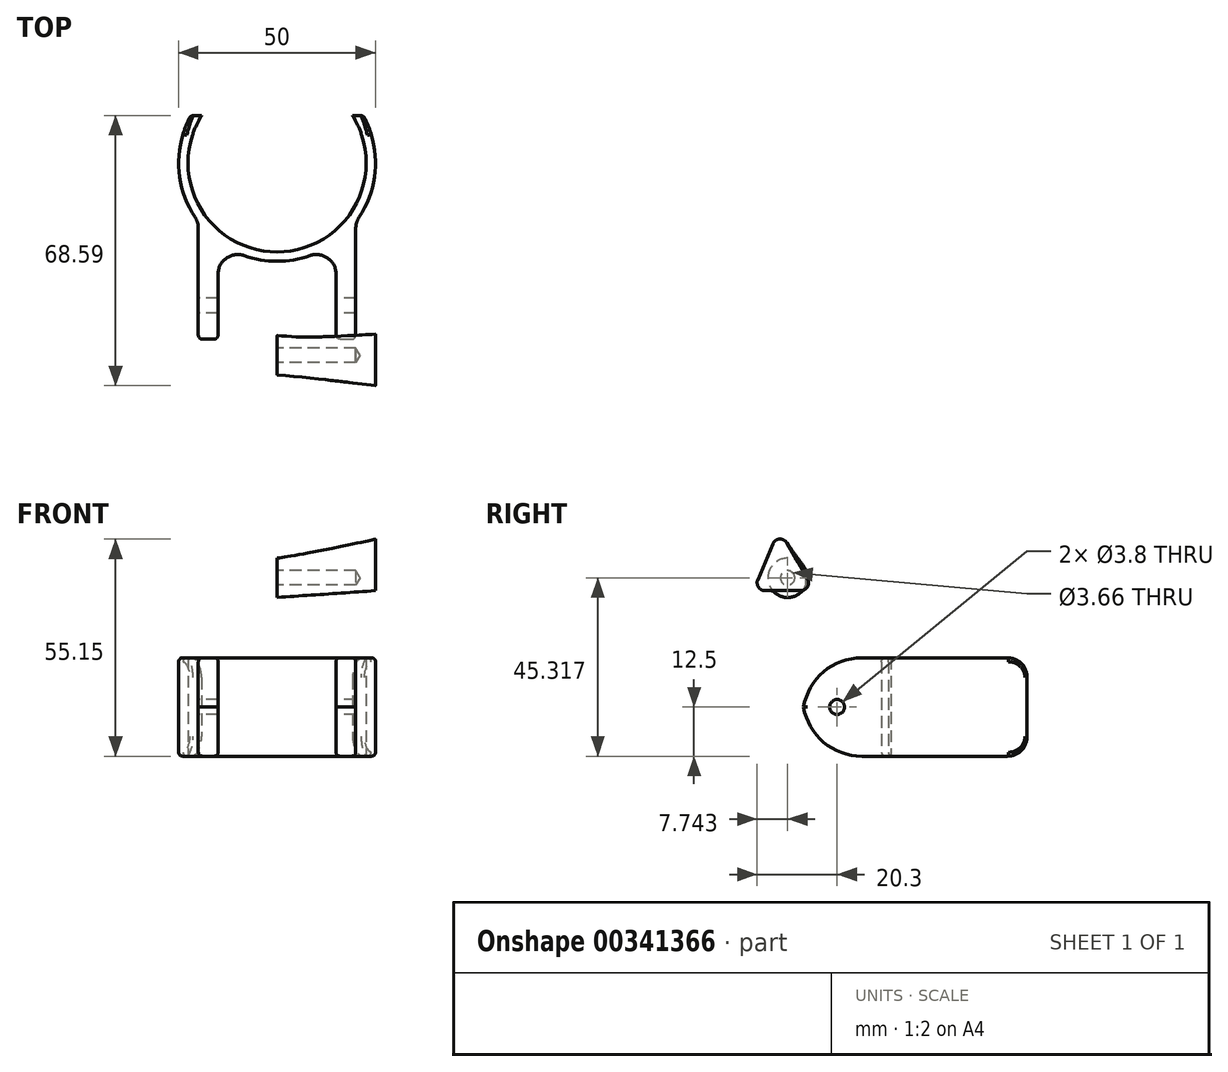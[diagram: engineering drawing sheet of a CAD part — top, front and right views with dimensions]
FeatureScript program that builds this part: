
annotation { "Feature Type Name" : "Feature", "Feature Type Description" : "" }
export const myFeature = defineFeature(function(context is Context, id is Id, definition is map)
    precondition{}
    {
        {
            var Q0;
            Q0=qCreatedBy(makeId("Top.planeOp"),FACE);
            var sketch = newSketch(context, id + "F0", { "sketchPlane" : qUnion([Q0])});
            skArc(sketch, "E0", {"start": v(-19.18, 12) * mm, "mid": v(0, -22.62) * mm, "end": v(19.18, 12) * mm});
            skArc(sketch, "E1", {"start": v(-21.93, 12) * mm, "mid": v(0, -25) * mm, "end": v(21.93, 12) * mm});
            skLineSegment(sketch, "E2", {"start": v(-19.18, 12) * mm, "end": v(-21.93, 12) * mm});
            skLineSegment(sketch, "E3", {"start": v(19.18, 12) * mm, "end": v(21.93, 12) * mm});
            skSolve(sketch);
        }
        {
            var Q0;
            Q0=makeQuery(id+"F0.imprint","IMPRINT",FACE,{"disambiguationData":[TD([[makeQuery(id+"F0.imprint","IMPRINT",EDGE,{"derivedFrom":sQuery(id+"F0.wireOp",EDGE,"E0")}),-1.0]])]});
            extrude(context, id + "F1", {"entities" : qUnion([Q0]), "depth" : 25 * mm});
        }
        {
            var Q0;
            Q0=qCreatedBy(makeId("Front.planeOp"),FACE);
            var sketch = newSketch(context, id + "F2", { "sketchPlane" : qUnion([Q0])});
            skLineSegment(sketch, "E4.bottom", {"start": v(-20, 25) * mm, "end": v(-15, 25) * mm});
            skLineSegment(sketch, "E4.top", {"start": v(-20, 0) * mm, "end": v(-15, 0) * mm});
            skLineSegment(sketch, "E4.left", {"start": v(-20, 25) * mm, "end": v(-20, 0) * mm});
            skLineSegment(sketch, "E4.right", {"start": v(-15, 25) * mm, "end": v(-15, 0) * mm});
            skLineSegment(sketch, "E5.bottom", {"start": v(15, 25) * mm, "end": v(20, 25) * mm});
            skLineSegment(sketch, "E5.top", {"start": v(15, 0) * mm, "end": v(20, 0) * mm});
            skLineSegment(sketch, "E5.left", {"start": v(15, 25) * mm, "end": v(15, 0) * mm});
            skLineSegment(sketch, "E5.right", {"start": v(20, 25) * mm, "end": v(20, 0) * mm});
            skSolve(sketch);
        }
        {
            var Q0;
            Q0=makeQuery(id+"F2.imprint","IMPRINT",FACE,{"disambiguationData":[TD([[makeQuery(id+"F2.imprint","IMPRINT",EDGE,{"derivedFrom":sQuery(id+"F2.wireOp",EDGE,"E4.bottom")}),-1.0]])]});
            var Q1;
            Q1=makeQuery(id+"F2.imprint","IMPRINT",FACE,{"disambiguationData":[TD([[makeQuery(id+"F2.imprint","IMPRINT",EDGE,{"derivedFrom":sQuery(id+"F2.wireOp",EDGE,"E5.bottom")}),-1.0]])]});
            var Q2;
            Q2=makeQuery(id+"F1.opExtrude","SWEPT_FACE",FACE,{"disambiguationData":[OSD([sQuery(id+"F0.wireOp",EDGE,"E0")])]});
            extrude(context, id + "F3", {"entities" : qUnion([Q0, Q1]), "endBoundEntityFace" : qUnion([Q2]), "depth" : 45 * mm, "hasSecondDirection" : true, "secondDirectionBound" : BoundingType.UP_TO_NEXT, "secondDirectionOppositeDirection" : false, "secondDirectionDepth" : 25 * mm});
        }
        {
            var Q0;
            Q0=makeQuery(id+"F3.opExtrude","SWEPT_BODY",BODY,{"disambiguationData":[OSD([sQuery(id+"F2.wireOp",EDGE,"E5.bottom"),sQuery(id+"F2.wireOp",EDGE,"E5.top"),sQuery(id+"F2.wireOp",EDGE,"E5.left"),sQuery(id+"F2.wireOp",EDGE,"E5.right")])]});
            var Q1;
            Q1=makeQuery(id+"F3.opExtrude","SWEPT_BODY",BODY,{"disambiguationData":[OSD([sQuery(id+"F2.wireOp",EDGE,"E4.bottom"),sQuery(id+"F2.wireOp",EDGE,"E4.top"),sQuery(id+"F2.wireOp",EDGE,"E4.left"),sQuery(id+"F2.wireOp",EDGE,"E4.right")])]});
            var Q2;
            Q2=makeQuery(id+"F1.opExtrude","SWEPT_BODY",BODY,{"disambiguationData":[OSD([sQuery(id+"F0.wireOp",EDGE,"E0"),sQuery(id+"F0.wireOp",EDGE,"E1"),sQuery(id+"F0.wireOp",EDGE,"E2"),sQuery(id+"F0.wireOp",EDGE,"E3")])]});
            booleanBodies(context, id + "F4", {"operationType" : BooleanOperationType.UNION, "tools" : qUnion([Q0, Q1, Q2])});
        }
        {
            var Q0;
            Q0=makeQuery(id+"F3.opExtrude","CAP_EDGE",EDGE,{"disambiguationData":[OSD([sQuery(id+"F2.wireOp",EDGE,"E4.bottom")])],"isStart":false});
            var Q1;
            Q1=makeQuery(id+"F3.opExtrude","CAP_EDGE",EDGE,{"disambiguationData":[OSD([sQuery(id+"F2.wireOp",EDGE,"E5.bottom")])],"isStart":false});
            var Q2;
            Q2=makeQuery(id+"F3.opExtrude","CAP_EDGE",EDGE,{"disambiguationData":[OSD([sQuery(id+"F2.wireOp",EDGE,"E4.top")])],"isStart":false});
            var Q3;
            Q3=makeQuery(id+"F3.opExtrude","CAP_EDGE",EDGE,{"disambiguationData":[OSD([sQuery(id+"F2.wireOp",EDGE,"E5.top")])],"isStart":false});
            fillet(context, id + "F5", {"entities" : qUnion([Q0, Q1, Q2, Q3]), "radius" : 15 * mm, "tangentPropagation" : true, "allowEdgeOverflow" : false});
        }
        {
            var Q0;
            Q0=makeQuery(id+"F3.opExtrude","SWEPT_FACE",FACE,{"disambiguationData":[OSD([sQuery(id+"F2.wireOp",EDGE,"E4.left")])]});
            var sketch = newSketch(context, id + "F6", { "sketchPlane" : qUnion([Q0])});
            skPoint(sketch, "E6", {"position": v(36.29, 12.5) * mm});
            skLineSegment(sketch, "E7", {"start": v(15, 25) * mm, "end": v(15, 0) * mm, "construction": true});
            skPoint(sketch, "E8", {"position": v(15, 12.5) * mm});
            skSolve(sketch);
        }
        {
            var Q0;
            Q0=sQuery(id+"F6.wireOp",VERTEX,"E6");
            var Q1;
            Q1=makeQuery(id+"F3.opExtrude","SWEPT_BODY",BODY,{"disambiguationData":[OSD([sQuery(id+"F2.wireOp",EDGE,"E5.bottom"),sQuery(id+"F2.wireOp",EDGE,"E5.top"),sQuery(id+"F2.wireOp",EDGE,"E5.left"),sQuery(id+"F2.wireOp",EDGE,"E5.right")])]});
            hole(context, id + "F7", {"style" : HoleStyle.SIMPLE, "endStyle" : HoleEndStyle.THROUGH, "standardTappedOrClearance" : lookupTablePath({ "standard" : "ANSI", "fit" : "Normal (ASME)", "size" : "#6", "type" : "Clearance" }), "standardBlindInLast" : lookupTablePath({ "fit" : "Free", "standard" : "ANSI", "size" : "#6", "type" : "Clearance" }), "holeDiameter" : 3.8 * mm, "startFromSketch" : true, "locations" : qUnion([Q0]), "scope" : qUnion([Q1]), "isTappedThrough" : true});
        }
        {
            var Q0;
            Q0=qCreatedBy(makeId("Right.planeOp"),FACE);
            var sketch = newSketch(context, id + "F8", { "sketchPlane" : qUnion([Q0])});
            skCircle(sketch, "E9", {"center": v(-48.85, 45.32) * mm, "radius": 5 * mm});
            skSolve(sketch);
        }
        {
            var Q0;
            Q0=qCreatedBy(makeId("Right.planeOp"),FACE);
            cPlane(context, id + "F9", {"entities" : qUnion([Q0]), "cplaneType" : CPlaneType.OFFSET, "offset" : 25 * mm, "width" : 150 * mm, "height" : 150 * mm});
        }
        {
            var Q0;
            Q0=qCreatedBy(id+"F9.planeOp",FACE);
            var sketch = newSketch(context, id + "F10", { "sketchPlane" : qUnion([Q0])});
            skLineSegment(sketch, "E10.top", {"start": v(-54.59, 42.05) * mm, "end": v(-45.52, 42.05) * mm});
            skPoint(sketch, "E11", {"position": v(-51.05, 51.71) * mm});
            skPoint(sketch, "E11.positionSnap0", {"position": v(-51.05, 57.64) * mm});
            skPoint(sketch, "E11.positionSnap1", {"position": v(-42.55, 51.71) * mm});
            skLineSegment(sketch, "E12", {"start": v(-56.43, 44.82) * mm, "end": v(-52.61, 53.92) * mm});
            skLineSegment(sketch, "E13", {"start": v(-49.04, 54.15) * mm, "end": v(-43.78, 45.05) * mm});
            skPoint(sketch, "E10.left.start.orphan", {"position": v(-59.05, 53.9) * mm});
            skPoint(sketch, "E14.orphan", {"position": v(-43.05, 61.38) * mm});
            skPoint(sketch, "E15.visualSharp", {"position": v(-57.6, 42.05) * mm});
            skArc(sketch, "E15.filletArc", {"start": v(-56.43, 44.82) * mm, "mid": v(-56.25, 42.94) * mm, "end": v(-54.59, 42.05) * mm});
            skPoint(sketch, "E16.visualSharp", {"position": v(-42.05, 42.05) * mm});
            skArc(sketch, "E16.filletArc", {"start": v(-45.52, 42.05) * mm, "mid": v(-43.78, 43.05) * mm, "end": v(-43.78, 45.05) * mm});
            skArc(sketch, "E17.filletArc", {"start": v(-49.04, 54.15) * mm, "mid": v(-50.9, 55.14) * mm, "end": v(-52.61, 53.92) * mm});
            skSolve(sketch);
        }
        {
            var Q0;
            Q0=makeQuery(id+"F8.imprint","IMPRINT",FACE,{"disambiguationData":[TD([[makeQuery(id+"F8.imprint","IMPRINT",EDGE,{"derivedFrom":sQuery(id+"F8.wireOp",EDGE,"E9")}),1.0]])]});
            var Q1;
            Q1=makeQuery(id+"F10.imprint","IMPRINT",FACE,{"disambiguationData":[TD([[makeQuery(id+"F10.imprint","IMPRINT",EDGE,{"derivedFrom":sQuery(id+"F10.wireOp",EDGE,"E10.top")}),1.0]])]});
            loft(context, id + "F11", {"sheetProfilesArray" : [{ "sheetProfileEntities" : qUnion([Q0]) }, { "sheetProfileEntities" : qUnion([Q1]) }]});
        }
        {
            var Q0;
            Q0=sQuery(id+"F8.wireOp",VERTEX,"E9.center");
            var Q1;
            Q1=makeQuery(id+"F11.opLoft","SWEPT_BODY",BODY,{"disambiguationData":[OSD([makeQuery(id+"F8.imprint","IMPRINT",FACE,{"disambiguationData":[TD([[makeQuery(id+"F8.imprint","IMPRINT",EDGE,{"derivedFrom":sQuery(id+"F8.wireOp",EDGE,"E9")}),1.0]])]}),makeQuery(id+"F10.imprint","IMPRINT",FACE,{"disambiguationData":[TD([[makeQuery(id+"F10.imprint","IMPRINT",EDGE,{"derivedFrom":sQuery(id+"F10.wireOp",EDGE,"E10.bottom")}),-1.0]])]})])]});
            hole(context, id + "F12", {"style" : HoleStyle.SIMPLE, "endStyle" : HoleEndStyle.BLIND, "oppositeDirection" : true, "standardTappedOrClearance" : lookupTablePath({ "standard" : "ANSI", "fit" : "Close", "size" : "#6", "type" : "Clearance" }), "standardBlindInLast" : lookupTablePath({ "fit" : "Close", "standard" : "ANSI", "size" : "#6", "type" : "Clearance" }), "holeDiameter" : 3.66 * mm, "holeDepth" : 20 * mm, "startFromSketch" : true, "locations" : qUnion([Q0]), "scope" : qUnion([Q1])});
        }
        {
            var Q0;
            Q0=makeQuery(id+"F1.opExtrude","CAP_EDGE",EDGE,{"disambiguationData":[OSD([sQuery(id+"F0.wireOp",EDGE,"E2")])],"isStart":false});
            var Q1;
            Q1=makeQuery(id+"F1.opExtrude","CAP_EDGE",EDGE,{"disambiguationData":[OSD([sQuery(id+"F0.wireOp",EDGE,"E2")])],"isStart":true});
            var Q2;
            Q2=makeQuery(id+"F1.opExtrude","CAP_EDGE",EDGE,{"disambiguationData":[OSD([sQuery(id+"F0.wireOp",EDGE,"E3")])],"isStart":true});
            var Q3;
            Q3=makeQuery(id+"F1.opExtrude","CAP_EDGE",EDGE,{"disambiguationData":[OSD([sQuery(id+"F0.wireOp",EDGE,"E3")])],"isStart":false});
            var Q4;
            Q4=makeQuery(id+"F4.opBoolean","INTERSECT",EDGE,{"derivedFrom":[makeQuery(id+"F1.opExtrude","SWEPT_FACE",FACE,{"disambiguationData":[OSD([sQuery(id+"F0.wireOp",EDGE,"E1")])]}),makeQuery(id+"F3.opExtrude","SWEPT_FACE",FACE,{"disambiguationData":[OSD([sQuery(id+"F2.wireOp",EDGE,"E4.right")])]})]});
            var Q5;
            Q5=makeQuery(id+"F4.opBoolean","INTERSECT",EDGE,{"derivedFrom":[makeQuery(id+"F1.opExtrude","SWEPT_FACE",FACE,{"disambiguationData":[OSD([sQuery(id+"F0.wireOp",EDGE,"E1")])]}),makeQuery(id+"F3.opExtrude","SWEPT_FACE",FACE,{"disambiguationData":[OSD([sQuery(id+"F2.wireOp",EDGE,"E5.left")])]})]});
            var Q6;
            Q6=makeQuery(id+"F4.opBoolean","INTERSECT",EDGE,{"derivedFrom":[makeQuery(id+"F1.opExtrude","SWEPT_FACE",FACE,{"disambiguationData":[OSD([sQuery(id+"F0.wireOp",EDGE,"E1")])]}),makeQuery(id+"F3.opExtrude","SWEPT_FACE",FACE,{"disambiguationData":[OSD([sQuery(id+"F2.wireOp",EDGE,"E4.left")])]})]});
            var Q7;
            Q7=makeQuery(id+"F4.opBoolean","INTERSECT",EDGE,{"derivedFrom":[makeQuery(id+"F1.opExtrude","SWEPT_FACE",FACE,{"disambiguationData":[OSD([sQuery(id+"F0.wireOp",EDGE,"E1")])]}),makeQuery(id+"F3.opExtrude","SWEPT_FACE",FACE,{"disambiguationData":[OSD([sQuery(id+"F2.wireOp",EDGE,"E5.right")])]})]});
            fillet(context, id + "F13", {"entities" : qUnion([Q0, Q1, Q2, Q3, Q4, Q5, Q6, Q7]), "radius" : 5 * mm, "tangentPropagation" : true, "allowEdgeOverflow" : false});
        }
        {
            var Q0;
            {var subQ0=sQuery(id+"F0.wireOp",EDGE,"E1");var subQ1=sQuery(id+"F0.wireOp",EDGE,"E2");Q0=makeQuery(id+"F4.opBoolean","SPLIT",EDGE,{"disambiguationData":[TD([makeQuery(id+"F1.opExtrude","SWEPT_FACE",FACE,{"disambiguationData":[OSD([subQ1])]})])],"derivedFrom":makeQuery(id+"F1.opExtrude","CAP_EDGE",EDGE,{"disambiguationData":[OSD([subQ0])],"isStart":true})});}
            var Q1;
            Q1=makeQuery(id+"F5.opFillet","BLEND_EDGE",EDGE,{"blendedFrom":[makeQuery(id+"F3.opExtrude","CAP_EDGE",EDGE,{"disambiguationData":[OSD([sQuery(id+"F2.wireOp",EDGE,"E4.top")])],"isStart":false}),makeQuery(id+"F3.opExtrude","SWEPT_FACE",FACE,{"disambiguationData":[OSD([sQuery(id+"F2.wireOp",EDGE,"E4.left")])]})],"blendedInto":[makeQuery(id+"F3.opExtrude","SWEPT_FACE",FACE,{"disambiguationData":[OSD([sQuery(id+"F2.wireOp",EDGE,"E4.left")])]})]});
            var Q2;
            {var subQ0=sQuery(id+"F0.wireOp",EDGE,"E2");var subQ1=sQuery(id+"F0.wireOp",EDGE,"E1");Q2=makeQuery(id+"F4.opBoolean","SPLIT",EDGE,{"disambiguationData":[TD([makeQuery(id+"F1.opExtrude","SWEPT_FACE",FACE,{"disambiguationData":[OSD([subQ0])]})])],"derivedFrom":makeQuery(id+"F1.opExtrude","CAP_EDGE",EDGE,{"disambiguationData":[OSD([subQ1])],"isStart":false})});}
            var Q3;
            Q3=makeQuery(id+"F3.opExtrude","SWEPT_EDGE",EDGE,{"disambiguationData":[OSD([sQuery(id+"F2.wireOp",EDGE,"E4.bottom"),sQuery(id+"F2.wireOp",EDGE,"E4.left")])]});
            var Q4;
            {var subQ0=sQuery(id+"F0.wireOp",EDGE,"E1");Q4=makeQuery(id+"F4.opBoolean","SPLIT",EDGE,{"disambiguationData":[TD([makeQuery(id+"F3.opExtrude","SWEPT_FACE",FACE,{"disambiguationData":[OSD([sQuery(id+"F2.wireOp",EDGE,"E4.right")])]})])],"derivedFrom":makeQuery(id+"F1.opExtrude","CAP_EDGE",EDGE,{"disambiguationData":[OSD([subQ0])],"isStart":false})});}
            var Q5;
            {var subQ0=sQuery(id+"F0.wireOp",EDGE,"E3");var subQ2=sQuery(id+"F0.wireOp",EDGE,"E1");Q5=makeQuery(id+"F4.opBoolean","SPLIT",FACE,{"disambiguationData":[TD([makeQuery(id+"F1.opExtrude","SWEPT_FACE",FACE,{"disambiguationData":[OSD([subQ0])]})])],"derivedFrom":makeQuery(id+"F1.opExtrude","SWEPT_FACE",FACE,{"disambiguationData":[OSD([subQ2])]})});}
            var Q6;
            Q6=makeQuery(id+"F4.opBoolean","INTERSECT",EDGE,{"derivedFrom":[makeQuery(id+"F1.opExtrude","SWEPT_FACE",FACE,{"disambiguationData":[OSD([sQuery(id+"F0.wireOp",EDGE,"E1")])]}),makeQuery(id+"F3.opExtrude","SWEPT_FACE",FACE,{"disambiguationData":[OSD([sQuery(id+"F2.wireOp",EDGE,"E4.left")])]})]});
            var Q7;
            Q7=makeQuery(id+"F5.opFillet","BLEND_EDGE",EDGE,{"blendedFrom":[makeQuery(id+"F3.opExtrude","CAP_EDGE",EDGE,{"disambiguationData":[OSD([sQuery(id+"F2.wireOp",EDGE,"E5.top")])],"isStart":false}),makeQuery(id+"F3.opExtrude","SWEPT_FACE",FACE,{"disambiguationData":[OSD([sQuery(id+"F2.wireOp",EDGE,"E5.left")])]})],"blendedInto":[makeQuery(id+"F3.opExtrude","SWEPT_FACE",FACE,{"disambiguationData":[OSD([sQuery(id+"F2.wireOp",EDGE,"E5.left")])]})]});
            var Q8;
            Q8=makeQuery(id+"F5.opFillet","BLEND_EDGE",EDGE,{"blendedFrom":[makeQuery(id+"F3.opExtrude","CAP_EDGE",EDGE,{"disambiguationData":[OSD([sQuery(id+"F2.wireOp",EDGE,"E5.bottom")])],"isStart":false}),makeQuery(id+"F3.opExtrude","SWEPT_FACE",FACE,{"disambiguationData":[OSD([sQuery(id+"F2.wireOp",EDGE,"E5.left")])]})],"blendedInto":[makeQuery(id+"F3.opExtrude","SWEPT_FACE",FACE,{"disambiguationData":[OSD([sQuery(id+"F2.wireOp",EDGE,"E5.left")])]})]});
            var Q9;
            Q9=makeQuery(id+"F5.opFillet","BLEND_EDGE",EDGE,{"blendedFrom":[makeQuery(id+"F3.opExtrude","CAP_EDGE",EDGE,{"disambiguationData":[OSD([sQuery(id+"F2.wireOp",EDGE,"E4.bottom")])],"isStart":false}),makeQuery(id+"F3.opExtrude","SWEPT_FACE",FACE,{"disambiguationData":[OSD([sQuery(id+"F2.wireOp",EDGE,"E4.right")])]})],"blendedInto":[makeQuery(id+"F3.opExtrude","SWEPT_FACE",FACE,{"disambiguationData":[OSD([sQuery(id+"F2.wireOp",EDGE,"E4.right")])]})]});
            var Q10;
            Q10=makeQuery(id+"F5.opFillet","BLEND_EDGE",EDGE,{"blendedFrom":[makeQuery(id+"F3.opExtrude","CAP_EDGE",EDGE,{"disambiguationData":[OSD([sQuery(id+"F2.wireOp",EDGE,"E4.top")])],"isStart":false}),makeQuery(id+"F3.opExtrude","SWEPT_FACE",FACE,{"disambiguationData":[OSD([sQuery(id+"F2.wireOp",EDGE,"E4.right")])]})],"blendedInto":[makeQuery(id+"F3.opExtrude","SWEPT_FACE",FACE,{"disambiguationData":[OSD([sQuery(id+"F2.wireOp",EDGE,"E4.right")])]})]});
            fillet(context, id + "F14", {"entities" : qUnion([Q0, Q1, Q2, Q3, Q4, Q5, Q6, Q7, Q8, Q9, Q10]), "radius" : 1 * mm, "tangentPropagation" : true, "allowEdgeOverflow" : false});
        }
    });
